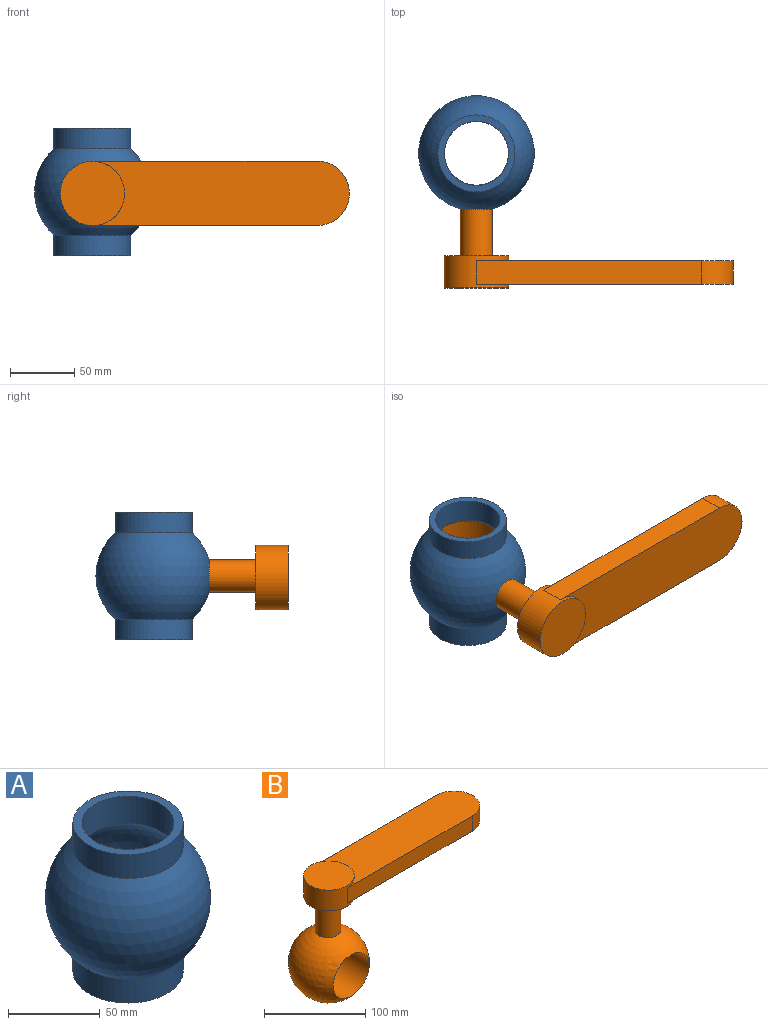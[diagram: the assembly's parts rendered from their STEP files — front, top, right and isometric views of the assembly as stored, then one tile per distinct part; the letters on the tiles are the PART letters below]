
ASSEMBLY  parts=2 mates=1
PART A: 9 faces, bbox 90x90x98.8 mm
  f0: cylinder r=25mm len=50mm, axis (0,0,1), area 2858.4mm2, adj f1,f7
  f1: plane 60x60mm, normal (0,0,1), area 863.9mm2, adj f0,f2
  f2: cylinder r=30mm len=60mm, axis (0,0,1), area 2993.6mm2, adj f1,f3
  f3: sphere r=45mm, area 18466.3mm2, adj f2,f4,f8
  f4: cylinder r=30mm len=60mm, axis (0,0,1), area 2993.6mm2, adj f3,f5
  f5: plane 60x60mm, normal (0,0,-1), area 863.9mm2, adj f4,f6
  f6: cylinder r=25mm len=50mm, axis (0,0,1), area 2858.4mm2, adj f5,f7
  f7: sphere r=40mm, area 15191.9mm2, adj f0,f6,f8
  f8: cylinder r=12.5mm len=25mm, axis (0,-1,0), area 410.9mm2, adj f3,f7
PART B: 12 faces, bbox 240x80x145 mm
  f0: sphere r=40mm, area 15191.6mm2, adj f1,f2
  f1: cylinder r=12.5mm len=42.39mm, axis (0,0,-1), area 3300.3mm2, adj f0,f5
  f2: cylinder r=25mm len=62.45mm, axis (0,1,0), area 9809.6mm2, adj f0
  f3: cylinder r=25mm len=50mm, axis (0,0,-1), area 2498mm2, adj f4,f5,f6,f7,f8,f9
  f4: plane 50x50mm, normal (0,0,1), area 1963.5mm2, adj f3
  f5: plane 50x50mm, normal (0,0,-1), area 1472.6mm2, adj f1,f3
  f6: plane 174.35x18.35mm, normal (0,-1,0), area 3198.7mm2, adj f3,f8,f9,f11
  f7: plane 18.35x0.01mm, normal (-1,0,0), area 0.2mm2, adj f3,f8,f9,f10
  f8: plane 200x50mm, normal (0,0,1), area 8750mm2, adj f3,f6,f7,f10,f11
  f9: plane 200x50mm, normal (0,0,-1), area 8750mm2, adj f3,f6,f7,f10,f11
  f10: plane 175x18.35mm, normal (0,1,0), area 3210.7mm2, adj f7,f8,f9,f11
  f11: cylinder r=25mm len=50mm, axis (0,0,-1), area 1441mm2, adj f6,f8,f9,f10
PLACE A rot(axis=(0,0,1),180deg) t=(3.36,-134.31,64.99)mm
PLACE B rot(axis=(1,0,0),90deg) t=(3.36,-133.95,63.88)mm
MATE revolute B.f1 <-> A.f8  axis (0,1,0) through (3.36,-171.31,64.99)mm
